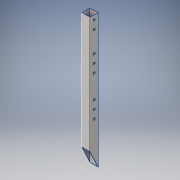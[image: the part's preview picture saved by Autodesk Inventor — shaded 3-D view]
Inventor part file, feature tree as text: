
AUTODESK INVENTOR PART (.ipt)
format: ipt  version: 2016 (Build 200138000, 138)  size: 155,136 bytes
history: native  units: in
note: dims shown in document units (in); Inventor stores cm internally (conversion verified against a paired STEP export)
features: sketch x5, extrude x4
ambient origin geometry x8: Origin, YZ Plane, XZ Plane, XY Plane, X Axis, Y Axis, Z Axis, Center Point
bodies: Solid1 (feature_tree)
feature tree (9):
  extrude  "Extrusion1"  Depth=1.0in
  extrude  "Extrusion2"  Depth=0.0625in TaperAngle=0.0deg
  extrude  "Extrusion3"  Depth=1.0in TaperAngle=0.0deg
  extrude  "Extrusion4"  Depth=0.5in
  sketch  "Sketch5"  dims[d10=0.5in d11=0.2656in d12=0.5in d13=1.5in d14=1.0in d15=0.0in d16=0.2656in d17=6.0in d18=0.2656in d19=1.0in d20=0.2656in d21=0.5in d22=0.5in d23=0.5in d24=1.0in d25=0.2656in d26=1.0in d27=1.0in d28=0.5in d30=10.75in d31=1.0in d32=0.0in]
  sketch  "Sketch1"  dims[d0=1.0in d1=1.0in]
  sketch  "Sketch2"  dims[d2=0.0625in d3=16.0in d4=0.0in]
  sketch  "Sketch3"  dims[d5=0.1718in d6=1.0in d7=0.0in]
  sketch  "Sketch4"  dims[d8=0.2656in d9=0.5in]
